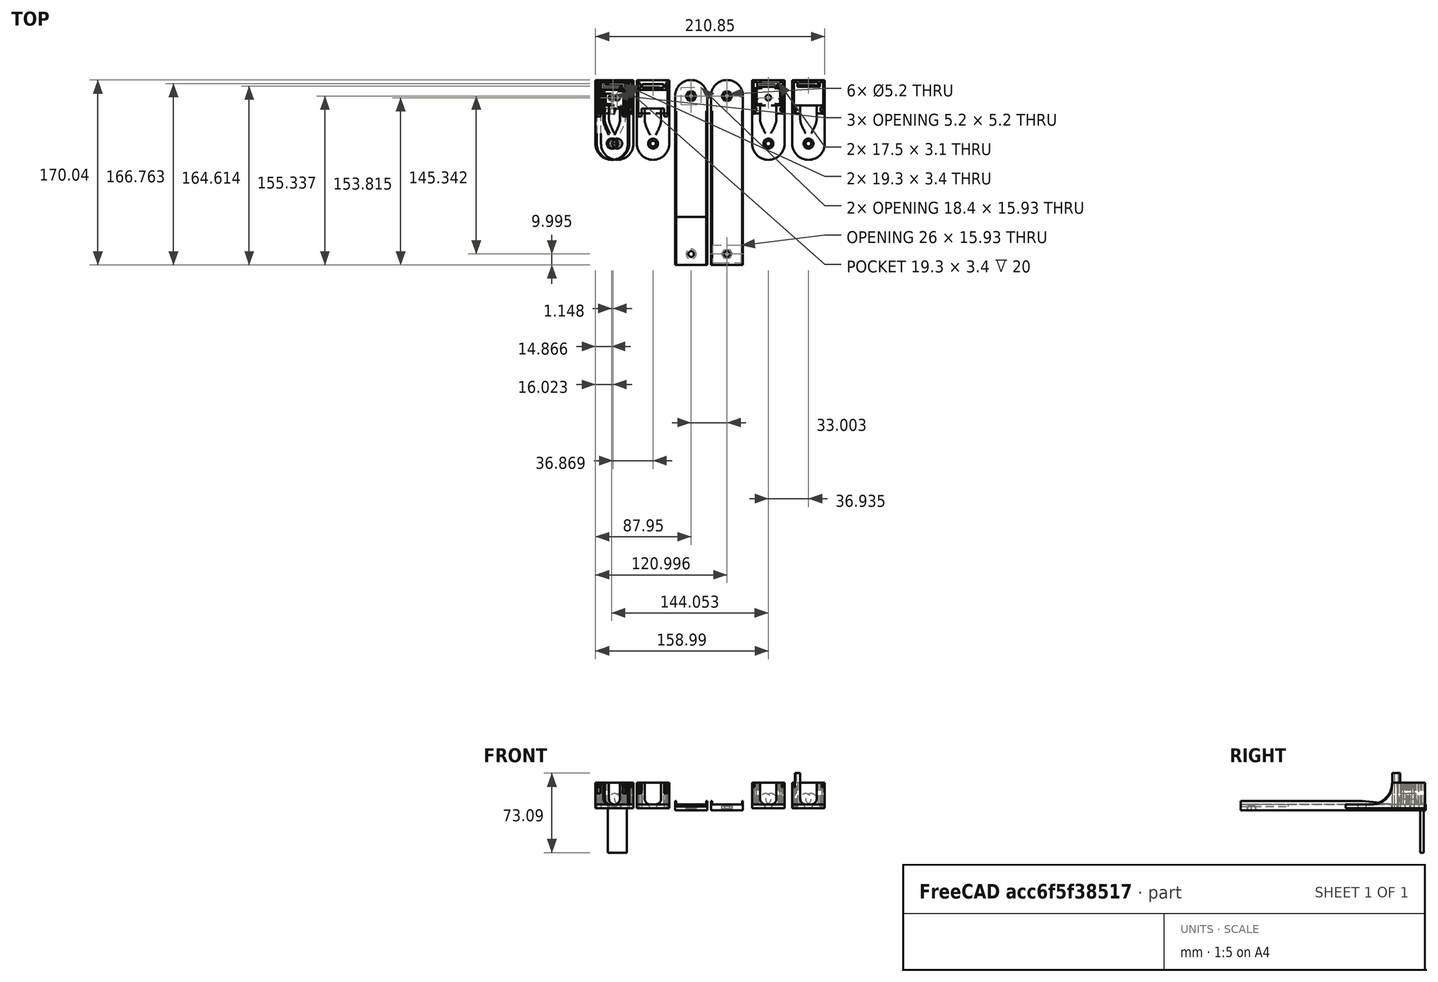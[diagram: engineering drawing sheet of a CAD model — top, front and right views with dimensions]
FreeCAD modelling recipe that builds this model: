
FCSTD DOCUMENT  (FreeCAD 0.18.4R)
Label: lamp.hanger.new
License: All rights reserved
LicenseURL: http://en.wikipedia.org/wiki/All_rights_reserved
objects: Part::Extrusion×23, Part::Cut×20, Part::Part2DObjectPython×19, Part::MultiFuse×12, Part::FeaturePython×10, Part::Feature×8, App::DocumentObjectGroup×3
note: 92 computed .brp shape members not serialized (recipe doc carries the construction recipe); baked Part::Feature solids carry a one-line shape summary decoded from their .brp

FEATURE [Part::MultiFuse] Fusion
FEATURE [Part::Part2DObjectPython] Circle  # Draft 2D object (typed FeaturePython)
  FirstAngle = 0
  LastAngle = 0
  MakeFace = true
  Placement = pos=(-707.421,-8.97512,-3.63395) rot=(0,0,1;0rad)
  Radius = 2.6
  Support = -> [Fusion]
FEATURE [Part::Extrusion] Extrusion
  Base = -> Circle
  Dir = (0,0,-104.516)
  DirMode = 0
  FaceMakerClass = Part::FaceMakerBullseye
  LengthFwd = 0
  LengthRev = 0
  Solid = true
  Symmetric = false
FEATURE [Part::Cut] Cut
  Base = -> Fusion
  Tool = -> Extrusion
FEATURE [Part::Part2DObjectPython] Rectangle  # Draft 2D object (typed FeaturePython)
  ChamferSize = 0
  Columns = 1
  FilletRadius = 0
  Height = 3.10055
  Length = 17.5
  MakeFace = true
  Placement = pos=(-716.1,2.42323,16.3661) rot=(0,0,1;0rad)
  Rows = 1
FEATURE [Part::Extrusion] Extrusion001
  Base = -> Rectangle
  Dir = (2.96e-14,4.57e-14,-64.3884)
  DirMode = 0
  FaceMakerClass = Part::FaceMakerBullseye
  LengthFwd = 0
  LengthRev = 0
  Solid = true
  Symmetric = false
FEATURE [Part::Cut] Cut004006005004002008019023005004
  Placement = pos=(-176.911,1.4e-14,3.6e-14) rot=(0,0,1;0rad)
FEATURE [Part::Part2DObjectPython] Rectangle001  # Draft 2D object (typed FeaturePython)
  ChamferSize = 0
  Columns = 1
  FilletRadius = 0
  Height = 3.10055
  Length = 17.5
  MakeFace = true
  Placement = pos=(-676.081,2.42323,25.0661) rot=(0,0,1;0rad)
  Rows = 1
FEATURE [Part::Extrusion] Extrusion002
  Base = -> Rectangle001
  Dir = (2.04e-14,3.15e-14,-44.3555)
  DirMode = 0
  FaceMakerClass = Part::FaceMakerBullseye
  LengthFwd = 0
  LengthRev = 0
  Solid = true
  Symmetric = false
FEATURE [Part::Cut] Cut004006005004002008019023005005
  Base = -> Cut004006005004002008019023005004
  Tool = -> Extrusion002
FEATURE [Part::Feature] Face
  shape: bbox 29.86 x 30.4 x 3e-07 mm, 1 faces, 0 solids (baked)
FEATURE [Part::Extrusion] Extrusion003
  Base = -> Face
  Dir = (1.2e-15,1.59e-14,-8.7)
  DirMode = 0
  FaceMakerClass = Part::FaceMakerBullseye
  LengthFwd = 0
  LengthRev = 0
  Solid = true
  Symmetric = false
FEATURE [Part::Cut] Cut004006005004002008019023005006
  Base = -> Cut004006005004002008019023005005
  Tool = -> Extrusion003
FEATURE [Part::Feature] Face001
  Placement = pos=(-176.911,1.4e-14,3.6e-14) rot=(0,0,1;0rad)
  shape: bbox 5 x 7.4 x 3e-07 mm, 1 faces, 0 solids (baked)
FEATURE [Part::Extrusion] Extrusion004
  Base = -> Face001
  Dir = (-2.51e-14,6.47e-14,-8.7)
  DirMode = 0
  FaceMakerClass = Part::FaceMakerBullseye
  LengthFwd = 0
  LengthRev = 0
  Solid = true
  Symmetric = false
FEATURE [Part::Feature] Face002
  Placement = pos=(-176.911,1.4e-14,3.6e-14) rot=(0,0,1;0rad)
  shape: bbox 5 x 7.4 x 3e-07 mm, 1 faces, 0 solids (baked)
FEATURE [Part::Extrusion] Extrusion005
  Base = -> Face002
  Dir = (2.184e-13,5.98e-14,-8.7)
  DirMode = 0
  FaceMakerClass = Part::FaceMakerBullseye
  LengthFwd = 0
  LengthRev = 0
  Solid = true
  Symmetric = false
FEATURE [Part::Cut] Cut004006005004002008019023005007
  Base = -> Cut004006005004002008019023005006
  Placement = pos=(135.846,-2.34e-13,1.41e-13) rot=(0,0,1;0rad)
  Tool = -> Extrusion005
FEATURE [Part::Cut] Cut004006005004002008019023005008
  Base = -> Cut004006005004002008019023005007
  Tool = -> Extrusion004
FEATURE [Part::Cut] Cut004006005004002008019023005014
FEATURE [Part::MultiFuse] Fusion002005
  Placement = pos=(86.8688,-7.1e-15,-1.78e-14) rot=(0,0,1;0rad)
FEATURE [Part::Feature] Face003
  Placement = pos=(86.8688,-7e-15,-1.8e-14) rot=(0,0,1;0rad)
  shape: bbox 3.179 x 4.601 x 4.951e-06 mm, 1 faces, 0 solids (baked)
FEATURE [Part::Extrusion] Extrusion006
  Base = -> Face003
  Dir = (1.13e-14,3.35e-14,-10.0532)
  DirMode = 0
  FaceMakerClass = Part::FaceMakerBullseye
  LengthFwd = 0
  LengthRev = 0
  Solid = true
  Symmetric = false
FEATURE [Part::Feature] Face004
  Placement = pos=(86.8688,-7e-15,-1.8e-14) rot=(0,0,1;0rad)
  shape: bbox 3.308 x 4.601 x 4.951e-06 mm, 1 faces, 0 solids (baked)
FEATURE [Part::Extrusion] Extrusion007
  Base = -> Face004
  Dir = (1.43e-14,4.44e-14,-13.335)
  DirMode = 0
  FaceMakerClass = Part::FaceMakerBullseye
  LengthFwd = 0
  LengthRev = 0
  Solid = true
  Symmetric = false
FEATURE [Part::Cut] Cut004006005004002008019023005015
  Base = -> Fusion002005
  Tool = -> Extrusion006
FEATURE [Part::Cut] Cut004006005004002008019023005016
  Base = -> Cut004006005004002008019023005015
  Tool = -> Extrusion007
FEATURE [Part::MultiFuse] Fusion005002002014004003003002009002010004002003006003008008004007002004006006004008003005011006
  Placement = pos=(-82.9949,0,-5e-15) rot=(0,0,1;0rad)
  Shapes = -> [Cut004006005004002008019023005007]
FEATURE [Part::MultiFuse] Fusion005002002014004003003002009002010004002003006003008008004007002004003
  Placement = pos=(-677.592,-2.54468,-4) rot=(0,0,1;0rad)
FEATURE [Part::Part2DObjectPython] Rectangle002  # Draft 2D object (typed FeaturePython)
  ChamferSize = 0
  Columns = 1
  FilletRadius = 0
  Height = 20
  Length = 5.5
  MakeFace = true
  Placement = pos=(-705.896,-12.7746,-3.63395) rot=(1,0,0;1.5708rad)
  Rows = 1
  Support = -> [Cut004006005004002008019023005014]
FEATURE [Part::Extrusion] Extrusion008
  Base = -> Rectangle002
  Dir = (6.992e-13,9.7,-2.2e-15)
  DirMode = 0
  FaceMakerClass = Part::FaceMakerBullseye
  LengthFwd = 0
  LengthRev = 0
  Solid = true
  Symmetric = false
FEATURE [Part::Cut] Cut004006005004002008019023005017
  Base = -> Cut004006005004002008019023005014
  Tool = -> Extrusion008
FEATURE [Part::Part2DObjectPython] Rectangle003  # Draft 2D object (typed FeaturePython)
  ChamferSize = 0
  Columns = 1
  FilletRadius = 0
  Height = 20
  Length = 5.5
  MakeFace = true
  Placement = pos=(-716.896,-12.7746,16.3661) rot=(0,0.707107,-0.707107;3.14159rad)
  Rows = 1
  Support = -> [Cut004006005004002008019023005017]
FEATURE [Part::Extrusion] Extrusion009
  Base = -> Rectangle003
  Dir = (6.24e-13,9.7,-4.3e-15)
  DirMode = 0
  FaceMakerClass = Part::FaceMakerBullseye
  LengthFwd = 0
  LengthRev = 0
  Solid = true
  Symmetric = false
FEATURE [Part::Cut] Cut004006005004002008019023005018
  Base = -> Cut004006005004002008019023005017
  Tool = -> Extrusion009
FEATURE [Part::Part2DObjectPython] Rectangle004  # Draft 2D object (typed FeaturePython)
  ChamferSize = 0
  Columns = 1
  FilletRadius = 0
  Height = 2
  Length = 2
  MakeFace = true
  Placement = pos=(-723.896,-12.7746,-1.63395) rot=(0,0.707107,-0.707107;3.14159rad)
  Rows = 1
  Support = -> [Cut004006005004002008019023005018]
FEATURE [Part::Part2DObjectPython] Circle001  # Draft 2D object (typed FeaturePython)
  FirstAngle = 0
  LastAngle = 0
  MakeFace = true
  Placement = pos=(-725.896,-12.7746,-1.63395) rot=(0,0.707107,-0.707107;3.14159rad)
  Radius = 2
  Support = -> [Cut004006005004002008019023005018]
FEATURE [Part::Extrusion] Extrusion010
  Base = -> Rectangle004
  Dir = (6.24e-13,9.7,-4.3e-15)
  DirMode = 0
  FaceMakerClass = Part::FaceMakerBullseye
  LengthFwd = 0
  LengthRev = 0
  Solid = true
  Symmetric = false
FEATURE [Part::Extrusion] Extrusion011
  Base = -> Circle001
  Dir = (6.367e-13,9.7,-2.2e-15)
  DirMode = 0
  FaceMakerClass = Part::FaceMakerBullseye
  LengthFwd = 0
  LengthRev = 0
  Solid = true
  Symmetric = false
FEATURE [Part::Cut] Cut004006005004002008019023005019
  Base = -> Extrusion010
  Tool = -> Extrusion011
FEATURE [Part::Part2DObjectPython] Rectangle005  # Draft 2D object (typed FeaturePython)
  ChamferSize = 0
  Columns = 1
  FilletRadius = 0
  Height = 2
  Length = 2
  MakeFace = true
  Placement = pos=(-720.396,-12.7746,-1.63395) rot=(0,0.707107,-0.707107;3.14159rad)
  Rows = 1
  Support = -> [Cut004006005004002008019023005018]
FEATURE [Part::Extrusion] Extrusion012
  Base = -> Rectangle005
  Dir = (6.24e-13,9.7,-4.3e-15)
  DirMode = 0
  FaceMakerClass = Part::FaceMakerBullseye
  LengthFwd = 0
  LengthRev = 0
  Solid = true
  Symmetric = false
FEATURE [Part::Part2DObjectPython] Circle002  # Draft 2D object (typed FeaturePython)
  FirstAngle = 0
  LastAngle = 0
  MakeFace = true
  Placement = pos=(-720.396,-12.7746,-1.63395) rot=(0,0.707107,-0.707107;3.14159rad)
  Radius = 2
  Support = -> [Extrusion012]
FEATURE [Part::Extrusion] Extrusion013
  Base = -> Circle002
  Dir = (6.367e-13,9.7,-2.2e-15)
  DirMode = 0
  FaceMakerClass = Part::FaceMakerBullseye
  LengthFwd = 0
  LengthRev = 0
  Solid = true
  Symmetric = false
FEATURE [Part::Cut] Cut004006005004002008019023005020
  Base = -> Extrusion012
  Tool = -> Extrusion013
FEATURE [Part::MultiFuse] Fusion005002002014004003003002009002010004002003006003008008004007002004006006004008003005011007
  Shapes = -> [Cut004006005004002008019023005019,Cut004006005004002008019023005020,Cut004006005004002008019023005018]
FEATURE [Part::Part2DObjectPython] Rectangle006  # Draft 2D object (typed FeaturePython)
  ChamferSize = 0
  Columns = 1
  FilletRadius = 0
  Height = 2
  Length = 2
  MakeFace = true
  Placement = pos=(-702.396,-12.7746,-3.63395) rot=(1,0,0;1.5708rad)
  Rows = 1
  Support = -> [Fusion005002002014004003003002009002010004002003006003008008004007002004006006004008003005011007]
FEATURE [Part::Part2DObjectPython] Circle003  # Draft 2D object (typed FeaturePython)
  FirstAngle = 0
  LastAngle = 0
  MakeFace = true
  Placement = pos=(-702.396,-12.7746,-1.63395) rot=(1,0,0;1.5708rad)
  Radius = 2
  Support = -> [Rectangle006]
FEATURE [Part::Part2DObjectPython] Rectangle007  # Draft 2D object (typed FeaturePython)
  ChamferSize = 0
  Columns = 1
  FilletRadius = 0
  Height = 2
  Length = 2
  MakeFace = true
  Placement = pos=(-698.896,-12.7746,-3.63395) rot=(1,0,0;1.5708rad)
  Rows = 1
FEATURE [Part::Part2DObjectPython] Circle004  # Draft 2D object (typed FeaturePython)
  FirstAngle = 0
  LastAngle = 0
  MakeFace = true
  Placement = pos=(-696.896,-12.7746,-1.63395) rot=(1,0,0;1.5708rad)
  Radius = 2
  Support = -> [Fusion005002002014004003003002009002010004002003006003008008004007002004006006004008003005011007]
FEATURE [Part::Extrusion] Extrusion014
  Base = -> Rectangle006
  Dir = (6.992e-13,9.7,-2.2e-15)
  DirMode = 0
  FaceMakerClass = Part::FaceMakerBullseye
  LengthFwd = 0
  LengthRev = 0
  Solid = true
  Symmetric = false
FEATURE [Part::Extrusion] Extrusion015
  Base = -> Rectangle007
  Dir = (6.992e-13,9.7,-2.2e-15)
  DirMode = 0
  FaceMakerClass = Part::FaceMakerBullseye
  LengthFwd = 0
  LengthRev = 0
  Solid = true
  Symmetric = false
FEATURE [Part::Extrusion] Extrusion016
  Base = -> Circle004
  Dir = (6.992e-13,9.7,-2.2e-15)
  DirMode = 0
  FaceMakerClass = Part::FaceMakerBullseye
  LengthFwd = 0
  LengthRev = 0
  Solid = true
  Symmetric = false
FEATURE [Part::Extrusion] Extrusion017
  Base = -> Circle003
  Dir = (6.992e-13,9.7,-2.2e-15)
  DirMode = 0
  FaceMakerClass = Part::FaceMakerBullseye
  LengthFwd = 0
  LengthRev = 0
  Solid = true
  Symmetric = false
FEATURE [Part::Cut] Cut004006005004002008019023005021
  Base = -> Extrusion014
  Tool = -> Extrusion017
FEATURE [Part::Cut] Cut004006005004002008019023005022
  Base = -> Extrusion015
  Tool = -> Extrusion016
FEATURE [Part::MultiFuse] Fusion005002002014004003003002009002010004002003006003008008004007002004006006004008003005011008
  Shapes = -> [Cut004006005004002008019023005022,Fusion005002002014004003003002009002010004002003006003008008004007002004006006004008003005011007,Cut004006005004002008019023005021]
FEATURE [Part::Feature] Face005
  Placement = pos=(-756.265,0.89093,29.4029) rot=(1,0,0;1.5708rad)
  shape: bbox 4.243e-07 x 5 x 4 mm, 1 faces, 0 solids (baked)
FEATURE [Part::Extrusion] Extrusion018
  Base = -> Face005
  Dir = (0.5,-3.05e-14,0)
  DirMode = 0
  FaceMakerClass = Part::FaceMakerBullseye
  LengthFwd = 0
  LengthRev = 0
  Solid = true
  Symmetric = false
FEATURE [Part::Cut] Cut004006005004002008019023005023
  Base = -> Fusion005002002014004003003002009002010004002003006003008008004007002004006006004008003005011008
  Tool = -> Extrusion018
FEATURE [Part::Feature] Face006
  Placement = pos=(-756.265,0.89093,29.4029) rot=(1,0,0;1.5708rad)
  shape: bbox 4.243e-07 x 5.5 x 4 mm, 1 faces, 0 solids (baked)
FEATURE [Part::Extrusion] Extrusion019
  Base = -> Face006
  Dir = (-0.5,3.05e-14,0)
  DirMode = 0
  FaceMakerClass = Part::FaceMakerBullseye
  LengthFwd = 0
  LengthRev = 0
  Solid = true
  Symmetric = false
FEATURE [Part::Cut] Cut004006005004002008019023005024
  Base = -> Cut004006005004002008019023005023
  Tool = -> Extrusion019
FEATURE [Part::Part2DObjectPython] Rectangle008  # Draft 2D object (typed FeaturePython)
  ChamferSize = 0
  Columns = 1
  FilletRadius = 0
  Height = 8.73003
  Length = 8.98196
  MakeFace = true
  Placement = pos=(-698.896,-12.7746,7.63603) rot=(0.57735,0.57735,0.57735;2.0944rad)
  Rows = 1
FEATURE [Part::FeaturePython] Slice  # WARN: FeaturePython — macro-defined, semantics opaque (R4)
  Base = -> Cut004006005004002008019023005024
  Mode = 1
  Tolerance = 0
  Tools = -> [Rectangle008]
FEATURE [Part::FeaturePython] Slice_child0  label="Slice.0"  # WARN: FeaturePython — macro-defined, semantics opaque (R4)
  Base = -> Slice
  FilterType = 1
  Invert = false
  OverrideMaxVal = 0
  WindowFrom = 80
  WindowTo = 100
  items = 0
FEATURE [App::DocumentObjectGroup] GrExplode_Slice  label="Exploded Slice"
  Group = -> [Slice_child0]
FEATURE [Part::FeaturePython] Slice_child1  label="Slice.1"  # WARN: FeaturePython — macro-defined, semantics opaque (R4)
  Base = -> Slice
  FilterType = 1
  Invert = false
  OverrideMaxVal = 0
  Placement = pos=(0,0,-1) rot=(0,0,1;0rad)
  WindowFrom = 80
  WindowTo = 100
  items = 1
FEATURE [Part::Part2DObjectPython] Rectangle009  # Draft 2D object (typed FeaturePython)
  ChamferSize = 0
  Columns = 1
  FilletRadius = 0
  Height = 8.52247
  Length = 8.85872
  MakeFace = true
  Placement = pos=(-723.896,-3.91585,7.84359) rot=(0.57735,-0.57735,-0.57735;2.0944rad)
  Rows = 1
FEATURE [Part::FeaturePython] Slice001  # WARN: FeaturePython — macro-defined, semantics opaque (R4)
  Base = -> Slice_child0
  Mode = 1
  Tolerance = 0
  Tools = -> [Rectangle009]
FEATURE [Part::FeaturePython] Slice001_child0  label="Slice001.0"  # WARN: FeaturePython — macro-defined, semantics opaque (R4)
  Base = -> Slice001
  FilterType = 1
  Invert = false
  OverrideMaxVal = 0
  WindowFrom = 80
  WindowTo = 100
  items = 0
FEATURE [Part::FeaturePython] Slice001_child1  label="Slice001.1"  # WARN: FeaturePython — macro-defined, semantics opaque (R4)
  Base = -> Slice001
  FilterType = 1
  Invert = false
  OverrideMaxVal = 0
  Placement = pos=(0,0,-1) rot=(0,0,1;0rad)
  WindowFrom = 80
  WindowTo = 100
  items = 1
FEATURE [Part::MultiFuse] Fusion005002002014004003003002009002010004002003006003008008004007002004006006004008003005011009
  Shapes = -> [Slice001_child0,Slice001_child1]
FEATURE [Part::MultiFuse] Fusion005002002014004003003002009002010004002003006003008008004007002004006006004008003005011010
  Shapes = -> [Slice_child1,Fusion005002002014004003003002009002010004002003006003008008004007002004006006004008003005011009]
FEATURE [Part::Part2DObjectPython] Rectangle010  # Draft 2D object (typed FeaturePython)
  ChamferSize = 0
  Columns = 1
  FilletRadius = 0
  Height = 2
  Length = 0.991222
  MakeFace = true
  Placement = pos=(-724.887,-12.7746,-3.63395) rot=(1,0,0;1.5708rad)
  Rows = 1
  Support = -> [Fusion005002002014004003003002009002010004002003006003008008004007002004006006004008003005011010]
FEATURE [Part::Extrusion] Extrusion020
  Base = -> Rectangle010
  Dir = (6.243e-13,9.7,-4.3e-15)
  DirMode = 0
  FaceMakerClass = Part::FaceMakerBullseye
  LengthFwd = 0
  LengthRev = 0
  Solid = true
  Symmetric = false
FEATURE [Part::Cut] Cut004006005004002008019023005025
  Base = -> Fusion005002002014004003003002009002010004002003006003008008004007002004006006004008003005011010
  Tool = -> Extrusion020
FEATURE [Part::Part2DObjectPython] Rectangle011  # Draft 2D object (typed FeaturePython)
  ChamferSize = 0
  Columns = 1
  FilletRadius = 0
  Height = 2
  Length = 0.987131
  MakeFace = true
  Placement = pos=(-698.896,-12.7746,-3.63395) rot=(1,0,0;1.5708rad)
  Rows = 1
  Support = -> [Cut004006005004002008019023005025]
FEATURE [Part::Extrusion] Extrusion021
  Base = -> Rectangle011
  Dir = (6.995e-13,9.7,-2.2e-15)
  DirMode = 0
  FaceMakerClass = Part::FaceMakerBullseye
  LengthFwd = 0
  LengthRev = 0
  Solid = true
  Symmetric = false
FEATURE [Part::Cut] Cut004006005004002008019023005026
  Base = -> Cut004006005004002008019023005025
  Tool = -> Extrusion021
FEATURE [App::DocumentObjectGroup] GrExplode_Slice001  label="Exploded Slice001"
  Group = -> [Cut004006005004002008019023005026]
FEATURE [Part::Cut] Cut004006005004002008019023005046
  Placement = pos=(54.9167,-3.6e-15,-2.49e-14) rot=(0,0,1;0rad)
  Tool = -> Extrusion002
FEATURE [Part::Part2DObjectPython] Rectangle012  # Draft 2D object (typed FeaturePython)
  ChamferSize = 0
  Columns = 1
  FilletRadius = 0
  Height = 97.557
  Length = 40.1465
  MakeFace = true
  Placement = pos=(-654.539,-23.4762,21.6158) rot=(0,0.707107,-0.707107;3.14159rad)
  Rows = 1
  Support = -> [Cut004006005004002008019023005016]
FEATURE [Part::FeaturePython] Slice002  # WARN: FeaturePython — macro-defined, semantics opaque (R4)
  Base = -> Cut004006005004002008019023005016
  Mode = 1
  Tolerance = 0
  Tools = -> [Rectangle012]
FEATURE [Part::FeaturePython] Slice002_child1  label="Slice002.1"  # WARN: FeaturePython — macro-defined, semantics opaque (R4)
  Base = -> Slice002
  FilterType = 1
  Invert = false
  OverrideMaxVal = 0
  WindowFrom = 80
  WindowTo = 100
  items = 1
FEATURE [Part::FeaturePython] Slice002_child2  label="Slice002.2"  # WARN: FeaturePython — macro-defined, semantics opaque (R4)
  Base = -> Slice002
  FilterType = 1
  Invert = false
  OverrideMaxVal = 0
  WindowFrom = 80
  WindowTo = 100
  items = 2
FEATURE [Part::FeaturePython] Slice_child002  label="Slice.002"  # WARN: FeaturePython — macro-defined, semantics opaque (R4)
  Base = -> Slice
  FilterType = 1
  Invert = false
  OverrideMaxVal = 0
  WindowFrom = 80
  WindowTo = 100
  items = 1
FEATURE [Part::Feature] Slice_child002001  label="Slice.003"
  Placement = pos=(92.9335,0,-1.78e-14) rot=(0,0,1;0rad)
  shape: bbox 29.86 x 42.68 x 23.5 mm, 21 faces (baked)
FEATURE [Part::MultiFuse] Fusion005002002014004003003002009002010004002003006003008008004007002004006006004008003005011011
  Shapes = -> [Slice_child002001,Slice002_child2]
FEATURE [Part::MultiFuse] Fusion005002002014004003003002009002010004002003006003008008004007002004006006004008003005011012
  Shapes = -> [Fusion005002002014004003003002009002010004002003006003008008004007002004006006004008003005011011,Slice002_child1]
FEATURE [Part::Part2DObjectPython] Rectangle013  # Draft 2D object (typed FeaturePython)
  ChamferSize = 0
  Columns = 1
  FilletRadius = 0
  Height = 7
  Length = 5
  MakeFace = true
  Placement = pos=(-677.031,-18.8757,-3.63395) rot=(1,0,0;3.14159rad)
  Rows = 1
  Support = -> [Fusion005002002014004003003002009002010004002003006003008008004007002004006006004008003005011012]
FEATURE [Part::Extrusion] Extrusion022
  Base = -> Rectangle013
  Dir = (-3e-16,8e-16,-3.5)
  DirMode = 0
  FaceMakerClass = Part::FaceMakerBullseye
  LengthFwd = 0
  LengthRev = 0
  Solid = true
  Symmetric = false
FEATURE [Part::MultiFuse] Fusion005002002014004003003002009002010004002003006003008008004007002004006006004008003005011013
  Shapes = -> [Extrusion022,Fusion005002002014004003003002009002010004002003006003008008004007002004006006004008003005011012]
FEATURE [App::DocumentObjectGroup] GrExplode_Slice002  label="Exploded Slice002"
  Group = -> [Fusion005002002014004003003002009002010004002003006003008008004007002004006006004008003005011013]
FEATURE [Part::MultiFuse] Fusion005002002014004003003002009002010004002003006003008008004007002004006006004008003005011012024
  Placement = pos=(139,-7.1e-15,-2.75e-14) rot=(0,0,1;0rad)
  Shapes = -> [Slice001_child0]
